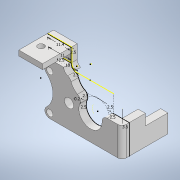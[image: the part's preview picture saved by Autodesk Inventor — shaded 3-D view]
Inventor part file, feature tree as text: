
AUTODESK INVENTOR PART (.ipt)
format: ipt  version: 2022 (Build 260153070, 153G)  size: 212,480 bytes
history: native  units: mm
features: reference x12, extrude x7, sketch x5, other x4, fillet x1, projected_geometry x1
ambient origin geometry x8: Origin, YZ Plane, XZ Plane, XY Plane, X Axis, Y Axis, Z Axis, Center Point
bodies: Solid1 (feature_tree)
feature tree (30):
  sketch  "Sketch1"  dims[d0=0.2mm d1=2.5mm]
  extrude  "Extrusion1"  Depth=2.5mm
  extrude  "Extrusion2"  Depth=10.0mm
  fillet  "Fillet1"  Radius=2.5mm
  extrude  "Extrusion3"  Depth=2.5mm
  sketch  "Sketch5"  dims[d6=2.5mm d7=2.5mm]
  extrude  "Extrusion4"  Depth=3.5mm TaperAngle=0.0deg
  extrude  "Extrusion5"  Depth=2.0mm
  extrude  "Extrusion6"  Depth=2.5mm
  extrude  "Extrusion7"  Depth=2.5mm
  reference  "Reference1"
  reference  "Reference2"
  reference  "Reference3"
  reference  "Reference4"
  reference  "Reference5"
  reference  "Reference6"
  reference  "Reference7"
  sketch  "Sketch2"  dims[d3=3.5mm d4=10.0mm d5=2.5mm]
  reference  "Reference8"
  reference  "Reference10"
  reference  "Reference11"
  projected_geometry  "Projected Loop1"
  sketch  "Sketch6"  dims[d8=2.5mm d9=3.5mm d10=0.0mm]
  reference  "Reference12"
  sketch  "Sketch7"  dims[d11=18.55mm d12=0.0mm d13=2.0mm d16=2.5mm d17=2.5mm d18=11.0mm d19=11.4mm d20=0.325mm d21=0.0mm d22=2.675mm d23=0.0mm d24=14.0mm d25=0.0mm d26=14.0mm d27=0.0mm d28=10.0mm d29=0.0mm]
  reference  "Reference13"
  other  "<userpath> laptop\Desktop\SumoBot\sumobotENCODER\MotorEncoderAssembly.iam"
  other  "MotorEncoderAssembly.iam"
  other  "TT motor output:1"
  other  "LM393 encoder:1"
